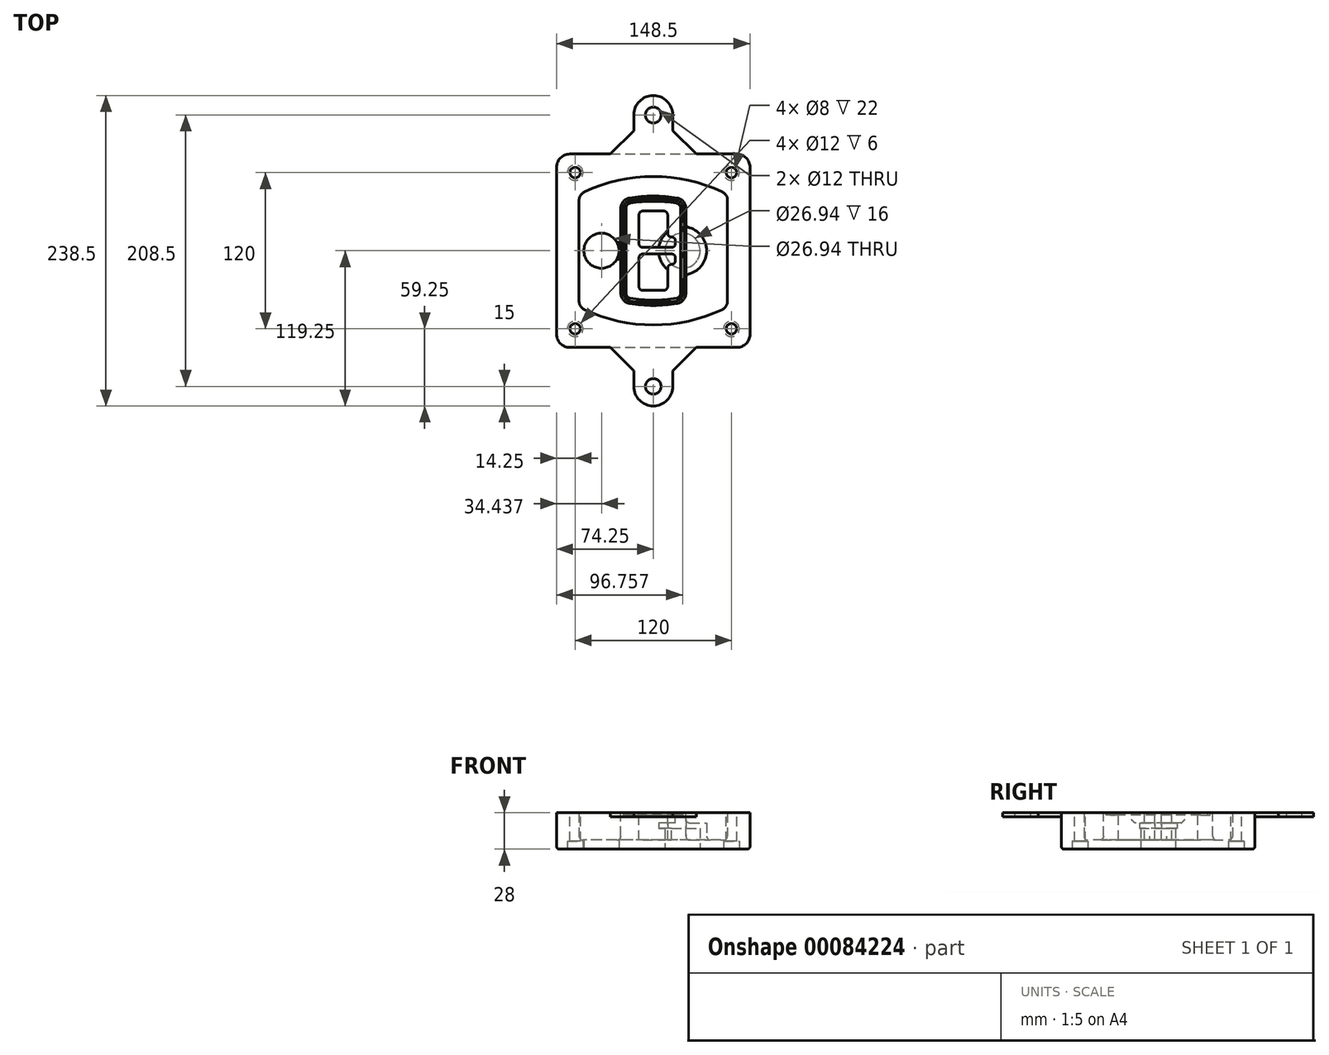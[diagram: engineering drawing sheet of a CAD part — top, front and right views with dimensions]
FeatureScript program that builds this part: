
annotation { "Feature Type Name" : "Feature", "Feature Type Description" : "" }
export const myFeature = defineFeature(function(context is Context, id is Id, definition is map)
    precondition{}
    {
        {
            var Q0;
            Q0=qCreatedBy(makeId("Top.planeOp"),FACE);
            var sketch = newSketch(context, id + "F0", { "sketchPlane" : qUnion([Q0])});
            skPoint(sketch, "E0.rect.middle", {"position": v(0, 0) * mm});
            skLineSegment(sketch, "E1.bottom", {"start": v(-64.25, -74.25) * mm, "end": v(64.25, -74.25) * mm});
            skLineSegment(sketch, "E1.top", {"start": v(-64.25, 74.25) * mm, "end": v(64.25, 74.25) * mm});
            skLineSegment(sketch, "E1.left", {"start": v(-74.25, -64.25) * mm, "end": v(-74.25, 64.25) * mm});
            skLineSegment(sketch, "E1.right", {"start": v(74.25, -64.25) * mm, "end": v(74.25, 64.25) * mm});
            skLineSegment(sketch, "E2", {"start": v(-74.25, 74.25) * mm, "end": v(74.25, -74.25) * mm, "construction": true});
            skLineSegment(sketch, "E3", {"start": v(74.25, 74.25) * mm, "end": v(-74.25, -74.25) * mm, "construction": true});
            skCircle(sketch, "E4", {"center": v(-60, 60) * mm, "radius": 4 * mm});
            skCircle(sketch, "E5", {"center": v(60, 60) * mm, "radius": 4 * mm});
            skCircle(sketch, "E6", {"center": v(60, -60) * mm, "radius": 4 * mm});
            skCircle(sketch, "E7", {"center": v(-60, -60) * mm, "radius": 4 * mm});
            skLineSegment(sketch, "E8", {"start": v(-60, 60) * mm, "end": v(60, 60) * mm, "construction": true});
            skLineSegment(sketch, "E9", {"start": v(60, 60) * mm, "end": v(60, -60) * mm, "construction": true});
            skLineSegment(sketch, "E10", {"start": v(60, -60) * mm, "end": v(-60, -60) * mm, "construction": true});
            skLineSegment(sketch, "E11", {"start": v(-60, -60) * mm, "end": v(-60, 60) * mm, "construction": true});
            skLineSegment(sketch, "E12", {"start": v(-60, 38.83) * mm, "end": v(-60, -38.83) * mm});
            skLineSegment(sketch, "E13", {"start": v(60, 38.83) * mm, "end": v(60, -38.83) * mm});
            skArc(sketch, "E14", {"start": v(54.26, 47.88) * mm, "mid": v(0, 60) * mm, "end": v(-54.26, 47.88) * mm});
            skArc(sketch, "E15", {"start": v(-54.26, -47.88) * mm, "mid": v(0, -60) * mm, "end": v(54.26, -47.88) * mm});
            skLineSegment(sketch, "E16", {"start": v(-60, 0) * mm, "end": v(60, 0) * mm, "construction": true});
            skPoint(sketch, "E17.visualSharp", {"position": v(-60, -45) * mm});
            skArc(sketch, "E17.filletArc", {"start": v(-60, -38.83) * mm, "mid": v(-58.44, -44.2) * mm, "end": v(-54.26, -47.88) * mm});
            skPoint(sketch, "E18.visualSharp", {"position": v(-60, 45) * mm});
            skArc(sketch, "E18.filletArc", {"start": v(-54.26, 47.88) * mm, "mid": v(-58.44, 44.2) * mm, "end": v(-60, 38.83) * mm});
            skPoint(sketch, "E19.visualSharp", {"position": v(60, 45) * mm});
            skArc(sketch, "E19.filletArc", {"start": v(60, 38.83) * mm, "mid": v(58.44, 44.2) * mm, "end": v(54.26, 47.88) * mm});
            skPoint(sketch, "E20.visualSharp", {"position": v(60, -45) * mm});
            skArc(sketch, "E20.filletArc", {"start": v(54.26, -47.88) * mm, "mid": v(58.44, -44.2) * mm, "end": v(60, -38.83) * mm});
            skPoint(sketch, "E21.visualSharp", {"position": v(-74.25, 74.25) * mm});
            skArc(sketch, "E21.filletArc", {"start": v(-64.25, 74.25) * mm, "mid": v(-71.32, 71.32) * mm, "end": v(-74.25, 64.25) * mm});
            skPoint(sketch, "E22.visualSharp", {"position": v(74.25, 74.25) * mm});
            skArc(sketch, "E22.filletArc", {"start": v(74.25, 64.25) * mm, "mid": v(71.32, 71.32) * mm, "end": v(64.25, 74.25) * mm});
            skPoint(sketch, "E23.visualSharp", {"position": v(74.25, -74.25) * mm});
            skArc(sketch, "E23.filletArc", {"start": v(64.25, -74.25) * mm, "mid": v(71.32, -71.32) * mm, "end": v(74.25, -64.25) * mm});
            skPoint(sketch, "E24.visualSharp", {"position": v(-74.25, -74.25) * mm});
            skArc(sketch, "E24.filletArc", {"start": v(-74.25, -64.25) * mm, "mid": v(-71.32, -71.32) * mm, "end": v(-64.25, -74.25) * mm});
            skArc(sketch, "E25.0", {"start": v(57, 38.83) * mm, "mid": v(55.9, 42.58) * mm, "end": v(52.98, 45.17) * mm});
            skLineSegment(sketch, "E25.1", {"start": v(57, 38.83) * mm, "end": v(57, -38.83) * mm});
            skArc(sketch, "E25.2", {"start": v(52.98, -45.17) * mm, "mid": v(55.9, -42.58) * mm, "end": v(57, -38.83) * mm});
            skArc(sketch, "E25.3", {"start": v(-52.98, -45.17) * mm, "mid": v(0, -57) * mm, "end": v(52.98, -45.17) * mm});
            skArc(sketch, "E25.4", {"start": v(-57, -38.83) * mm, "mid": v(-55.9, -42.58) * mm, "end": v(-52.98, -45.17) * mm});
            skArc(sketch, "E25.5", {"start": v(52.98, 45.17) * mm, "mid": v(0, 57) * mm, "end": v(-52.98, 45.17) * mm});
            skLineSegment(sketch, "E25.6", {"start": v(-57, 38.83) * mm, "end": v(-57, -38.83) * mm});
            skArc(sketch, "E25.7", {"start": v(-52.98, 45.17) * mm, "mid": v(-55.9, 42.58) * mm, "end": v(-57, 38.83) * mm});
            skArc(sketch, "E26.0", {"start": v(-55.96, 51.5) * mm, "mid": v(-61.82, 46.33) * mm, "end": v(-64, 38.83) * mm});
            skArc(sketch, "E26.1", {"start": v(55.96, 51.5) * mm, "mid": v(0, 64) * mm, "end": v(-55.96, 51.5) * mm});
            skArc(sketch, "E26.2", {"start": v(64, 38.83) * mm, "mid": v(61.82, 46.33) * mm, "end": v(55.96, 51.5) * mm});
            skLineSegment(sketch, "E26.3", {"start": v(64, 38.83) * mm, "end": v(64, -38.83) * mm});
            skArc(sketch, "E26.4", {"start": v(55.96, -51.5) * mm, "mid": v(61.82, -46.33) * mm, "end": v(64, -38.83) * mm});
            skLineSegment(sketch, "E26.5", {"start": v(-64, 38.83) * mm, "end": v(-64, -38.83) * mm});
            skArc(sketch, "E26.6", {"start": v(-55.96, -51.5) * mm, "mid": v(0, -64) * mm, "end": v(55.96, -51.5) * mm});
            skArc(sketch, "E26.7", {"start": v(-64, -38.83) * mm, "mid": v(-61.82, -46.33) * mm, "end": v(-55.96, -51.5) * mm});
            skSolve(sketch);
        }
        {
            var Q0;
            Q0=makeQuery(id+"F0.imprint","IMPRINT",FACE,{"disambiguationData":[TD([[makeQuery(id+"F0.imprint","IMPRINT",EDGE,{"derivedFrom":sQuery(id+"F0.wireOp",EDGE,"E1.bottom")}),1.0]])]});
            var Q1;
            Q1=makeQuery(id+"F0.imprint","IMPRINT",FACE,{"disambiguationData":[TD([[makeQuery(id+"F0.imprint","IMPRINT",EDGE,{"derivedFrom":sQuery(id+"F0.wireOp",EDGE,"E12")}),1.0]])]});
            var Q2;
            Q2=makeQuery(id+"F0.imprint","IMPRINT",FACE,{"disambiguationData":[TD([[makeQuery(id+"F0.imprint","IMPRINT",EDGE,{"derivedFrom":sQuery(id+"F0.wireOp",EDGE,"E25.0")}),1.0]])]});
            var Q3;
            Q3=makeQuery(id+"F0.imprint","IMPRINT",FACE,{"disambiguationData":[TD([[makeQuery(id+"F0.imprint","IMPRINT",EDGE,{"derivedFrom":sQuery(id+"F0.wireOp",EDGE,"E12")}),-1.0]])]});
            extrude(context, id + "F1", {"entities" : qUnion([Q0, Q1, Q2, Q3]), "oppositeDirection" : true, "depth" : 25 * mm});
        }
        {
            var Q0;
            Q0=makeQuery(id+"F0.imprint","IMPRINT",FACE,{"disambiguationData":[TD([[makeQuery(id+"F0.imprint","IMPRINT",EDGE,{"derivedFrom":sQuery(id+"F0.wireOp",EDGE,"E12")}),1.0]])]});
            extrude(context, id + "F2", {"entities" : qUnion([Q0]), "operationType" : NewBodyOperationType.ADD, "depth" : 3 * mm});
        }
        {
            var Q0;
            Q0=makeQuery(id+"F0.imprint","IMPRINT",FACE,{"disambiguationData":[TD([[makeQuery(id+"F0.imprint","IMPRINT",EDGE,{"derivedFrom":sQuery(id+"F0.wireOp",EDGE,"E25.0")}),1.0]])]});
            extrude(context, id + "F3", {"entities" : qUnion([Q0]), "operationType" : NewBodyOperationType.REMOVE, "oppositeDirection" : true, "depth" : 18 * mm});
        }
        {
            var Q0;
            Q0=makeQuery(id+"F2.opExtrude","CAP_FACE",FACE,{"disambiguationData":[OSD([sQuery(id+"F0.wireOp",EDGE,"E12"),sQuery(id+"F0.wireOp",EDGE,"E13"),sQuery(id+"F0.wireOp",EDGE,"E14"),sQuery(id+"F0.wireOp",EDGE,"E15"),sQuery(id+"F0.wireOp",EDGE,"E17.filletArc"),sQuery(id+"F0.wireOp",EDGE,"E18.filletArc"),sQuery(id+"F0.wireOp",EDGE,"E19.filletArc"),sQuery(id+"F0.wireOp",EDGE,"E20.filletArc"),sQuery(id+"F0.wireOp",EDGE,"E25.0"),sQuery(id+"F0.wireOp",EDGE,"E25.1"),sQuery(id+"F0.wireOp",EDGE,"E25.2"),sQuery(id+"F0.wireOp",EDGE,"E25.3"),sQuery(id+"F0.wireOp",EDGE,"E25.4"),sQuery(id+"F0.wireOp",EDGE,"E25.5"),sQuery(id+"F0.wireOp",EDGE,"E25.6"),sQuery(id+"F0.wireOp",EDGE,"E25.7")])],"isStart":false});
            var sketch = newSketch(context, id + "F4", { "sketchPlane" : qUnion([Q0])});
            skArc(sketch, "E27.0", {"start": v(-18.34, -40.45) * mm, "mid": v(0, -42) * mm, "end": v(18.34, -40.45) * mm});
            skArc(sketch, "E28.0", {"start": v(18.34, 40.45) * mm, "mid": v(0, 42) * mm, "end": v(-18.34, 40.45) * mm});
            skLineSegment(sketch, "E29", {"start": v(-25, 32.57) * mm, "end": v(-25, -32.57) * mm});
            skLineSegment(sketch, "E30", {"start": v(25, 32.57) * mm, "end": v(25, -32.57) * mm});
            skLineSegment(sketch, "E31", {"start": v(-25, 39.1) * mm, "end": v(25, 39.1) * mm, "construction": true});
            skLineSegment(sketch, "E32", {"start": v(-25, -39.1) * mm, "end": v(25, -39.1) * mm, "construction": true});
            skPoint(sketch, "E33.visualSharp", {"position": v(-25, 39.1) * mm});
            skArc(sketch, "E33.filletArc", {"start": v(-18.34, 40.45) * mm, "mid": v(-23.11, 37.73) * mm, "end": v(-25, 32.57) * mm});
            skPoint(sketch, "E34.visualSharp", {"position": v(25, 39.1) * mm});
            skArc(sketch, "E34.filletArc", {"start": v(25, 32.57) * mm, "mid": v(23.11, 37.73) * mm, "end": v(18.34, 40.45) * mm});
            skPoint(sketch, "E35.visualSharp", {"position": v(25, -39.1) * mm});
            skArc(sketch, "E35.filletArc", {"start": v(18.34, -40.45) * mm, "mid": v(23.11, -37.73) * mm, "end": v(25, -32.57) * mm});
            skPoint(sketch, "E36.visualSharp", {"position": v(-25, -39.1) * mm});
            skArc(sketch, "E36.filletArc", {"start": v(-25, -32.57) * mm, "mid": v(-23.11, -37.73) * mm, "end": v(-18.34, -40.45) * mm});
            skArc(sketch, "E37.0", {"start": v(52.98, 45.17) * mm, "mid": v(0, 57) * mm, "end": v(-52.98, 45.17) * mm});
            skArc(sketch, "E37.1", {"start": v(-52.98, 45.17) * mm, "mid": v(-55.9, 42.58) * mm, "end": v(-57, 38.83) * mm});
            skLineSegment(sketch, "E37.2", {"start": v(-57, 38.83) * mm, "end": v(-57, -38.83) * mm});
            skArc(sketch, "E37.3", {"start": v(-57, -38.83) * mm, "mid": v(-55.9, -42.58) * mm, "end": v(-52.98, -45.17) * mm});
            skArc(sketch, "E37.4", {"start": v(-52.98, -45.17) * mm, "mid": v(0, -57) * mm, "end": v(52.98, -45.17) * mm});
            skArc(sketch, "E37.5", {"start": v(52.98, -45.17) * mm, "mid": v(55.9, -42.58) * mm, "end": v(57, -38.83) * mm});
            skLineSegment(sketch, "E37.6", {"start": v(57, 38.83) * mm, "end": v(57, -38.83) * mm});
            skArc(sketch, "E37.7", {"start": v(57, 38.83) * mm, "mid": v(55.9, 42.58) * mm, "end": v(52.98, 45.17) * mm});
            skLineSegment(sketch, "E38.0", {"start": v(23, 32.57) * mm, "end": v(23, -32.57) * mm});
            skArc(sketch, "E38.1", {"start": v(18, -38.48) * mm, "mid": v(21.58, -36.44) * mm, "end": v(23, -32.57) * mm});
            skArc(sketch, "E38.2", {"start": v(-18, -38.48) * mm, "mid": v(0, -40) * mm, "end": v(18, -38.48) * mm});
            skArc(sketch, "E38.3", {"start": v(-23, -32.57) * mm, "mid": v(-21.58, -36.44) * mm, "end": v(-18, -38.48) * mm});
            skLineSegment(sketch, "E38.4", {"start": v(-23, 32.57) * mm, "end": v(-23, -32.57) * mm});
            skArc(sketch, "E38.5", {"start": v(23, 32.57) * mm, "mid": v(21.58, 36.44) * mm, "end": v(18, 38.48) * mm});
            skArc(sketch, "E38.6", {"start": v(-18, 38.48) * mm, "mid": v(-21.58, 36.44) * mm, "end": v(-23, 32.57) * mm});
            skArc(sketch, "E38.7", {"start": v(18, 38.48) * mm, "mid": v(0, 40) * mm, "end": v(-18, 38.48) * mm});
            skArc(sketch, "E39.0", {"start": v(21, 32.57) * mm, "mid": v(20.06, 35.15) * mm, "end": v(17.67, 36.5) * mm});
            skLineSegment(sketch, "E39.1", {"start": v(21, 32.57) * mm, "end": v(21, -32.57) * mm});
            skArc(sketch, "E39.2", {"start": v(17.67, -36.5) * mm, "mid": v(20.06, -35.15) * mm, "end": v(21, -32.57) * mm});
            skArc(sketch, "E39.3", {"start": v(-17.67, -36.5) * mm, "mid": v(0, -38) * mm, "end": v(17.67, -36.5) * mm});
            skArc(sketch, "E39.4", {"start": v(-21, -32.57) * mm, "mid": v(-20.06, -35.15) * mm, "end": v(-17.67, -36.5) * mm});
            skArc(sketch, "E39.5", {"start": v(17.67, 36.5) * mm, "mid": v(0, 38) * mm, "end": v(-17.67, 36.5) * mm});
            skLineSegment(sketch, "E39.6", {"start": v(-21, 32.57) * mm, "end": v(-21, -32.57) * mm});
            skArc(sketch, "E39.7", {"start": v(-17.67, 36.5) * mm, "mid": v(-20.06, 35.15) * mm, "end": v(-21, 32.57) * mm});
            skLineSegment(sketch, "E40", {"start": v(-25, 0) * mm, "end": v(25, 0) * mm, "construction": true});
            skLineSegment(sketch, "E41", {"start": v(-11, 5.5) * mm, "end": v(-11, 27.5) * mm});
            skLineSegment(sketch, "E42", {"start": v(-8, 30.5) * mm, "end": v(8, 30.5) * mm});
            skLineSegment(sketch, "E43", {"start": v(11, 27.5) * mm, "end": v(11, 13.5) * mm});
            skLineSegment(sketch, "E44", {"start": v(14, 10.5) * mm, "end": v(14, 10.5) * mm});
            skLineSegment(sketch, "E45", {"start": v(17, 7.5) * mm, "end": v(17, 5.5) * mm});
            skLineSegment(sketch, "E46", {"start": v(14, 2.5) * mm, "end": v(-8, 2.5) * mm});
            skPoint(sketch, "E47.visualSharp", {"position": v(-11, 30.5) * mm});
            skArc(sketch, "E47.filletArc", {"start": v(-8, 30.5) * mm, "mid": v(-10.12, 29.62) * mm, "end": v(-11, 27.5) * mm});
            skPoint(sketch, "E48.visualSharp", {"position": v(11, 30.5) * mm});
            skArc(sketch, "E48.filletArc", {"start": v(11, 27.5) * mm, "mid": v(10.12, 29.62) * mm, "end": v(8, 30.5) * mm});
            skPoint(sketch, "E49.visualSharp", {"position": v(11, 10.5) * mm});
            skArc(sketch, "E49.filletArc", {"start": v(11, 13.5) * mm, "mid": v(11.88, 11.38) * mm, "end": v(14, 10.5) * mm});
            skPoint(sketch, "E50.visualSharp", {"position": v(17, 10.5) * mm});
            skArc(sketch, "E50.filletArc", {"start": v(17, 7.5) * mm, "mid": v(16.12, 9.62) * mm, "end": v(14, 10.5) * mm});
            skPoint(sketch, "E51.visualSharp", {"position": v(17, 2.5) * mm});
            skArc(sketch, "E51.filletArc", {"start": v(14, 2.5) * mm, "mid": v(16.12, 3.38) * mm, "end": v(17, 5.5) * mm});
            skPoint(sketch, "E52.visualSharp", {"position": v(-11, 2.5) * mm});
            skArc(sketch, "E52.filletArc", {"start": v(-11, 5.5) * mm, "mid": v(-10.12, 3.38) * mm, "end": v(-8, 2.5) * mm});
            skLineSegment(sketch, "E53.0.MirrorCS", {"start": v(14, -2.5) * mm, "end": v(-8, -2.5) * mm});
            skArc(sketch, "E54.0.MirrorCS", {"start": v(-11, -5.5) * mm, "mid": v(-10.12, -3.38) * mm, "end": v(-8, -2.5) * mm});
            skLineSegment(sketch, "E55.0.MirrorCS", {"start": v(-11, -5.5) * mm, "end": v(-11, -27.5) * mm});
            skArc(sketch, "E56.0.MirrorCS", {"start": v(-8, -30.5) * mm, "mid": v(-10.12, -29.62) * mm, "end": v(-11, -27.5) * mm});
            skLineSegment(sketch, "E57.0.MirrorCS", {"start": v(-8, -30.5) * mm, "end": v(8, -30.5) * mm});
            skArc(sketch, "E58.0.MirrorCS", {"start": v(11, -27.5) * mm, "mid": v(10.12, -29.62) * mm, "end": v(8, -30.5) * mm});
            skLineSegment(sketch, "E59.0.MirrorCS", {"start": v(11, -27.5) * mm, "end": v(11, -13.5) * mm});
            skArc(sketch, "E60.0.MirrorCS", {"start": v(11, -13.5) * mm, "mid": v(11.88, -11.38) * mm, "end": v(14, -10.5) * mm});
            skArc(sketch, "E61.0.MirrorCS", {"start": v(17, -7.5) * mm, "mid": v(16.12, -9.62) * mm, "end": v(14, -10.5) * mm});
            skLineSegment(sketch, "E62.0.MirrorCS", {"start": v(17, -7.5) * mm, "end": v(17, -5.5) * mm});
            skArc(sketch, "E63.0.MirrorCS", {"start": v(14, -2.5) * mm, "mid": v(16.12, -3.38) * mm, "end": v(17, -5.5) * mm});
            skSolve(sketch);
        }
        {
            var Q0;
            Q0=makeQuery(id+"F4.imprint","IMPRINT",FACE,{"disambiguationData":[TD([[makeQuery(id+"F4.imprint","IMPRINT",EDGE,{"derivedFrom":sQuery(id+"F4.wireOp",EDGE,"E27.0")}),1.0]])]});
            var Q1;
            Q1=makeQuery(id+"F4.imprint","IMPRINT",FACE,{"disambiguationData":[TD([[makeQuery(id+"F4.imprint","IMPRINT",EDGE,{"derivedFrom":sQuery(id+"F4.wireOp",EDGE,"E38.0")}),-1.0]])]});
            var Q2;
            Q2=makeQuery(id+"F4.imprint","IMPRINT",FACE,{"disambiguationData":[TD([[makeQuery(id+"F4.imprint","IMPRINT",EDGE,{"derivedFrom":sQuery(id+"F4.wireOp",EDGE,"E39.0")}),1.0]])]});
            extrude(context, id + "F5", {"entities" : qUnion([Q0, Q1, Q2]), "operationType" : NewBodyOperationType.ADD, "endBound" : BoundingType.UP_TO_NEXT, "oppositeDirection" : true, "depth" : 25 * mm});
        }
        {
            var Q0;
            Q0=makeQuery(id+"F4.imprint","IMPRINT",FACE,{"disambiguationData":[TD([[makeQuery(id+"F4.imprint","IMPRINT",EDGE,{"derivedFrom":sQuery(id+"F4.wireOp",EDGE,"E38.0")}),-1.0]])]});
            extrude(context, id + "F6", {"entities" : qUnion([Q0]), "operationType" : NewBodyOperationType.REMOVE, "oppositeDirection" : true, "depth" : 2 * mm});
        }
        {
            var Q0;
            Q0=makeQuery(id+"F1.opExtrude","CAP_FACE",FACE,{"disambiguationData":[OSD([sQuery(id+"F0.wireOp",EDGE,"E1.bottom"),sQuery(id+"F0.wireOp",EDGE,"E1.top"),sQuery(id+"F0.wireOp",EDGE,"E1.left"),sQuery(id+"F0.wireOp",EDGE,"E1.right"),sQuery(id+"F0.wireOp",EDGE,"E4"),sQuery(id+"F0.wireOp",EDGE,"E5"),sQuery(id+"F0.wireOp",EDGE,"E6"),sQuery(id+"F0.wireOp",EDGE,"E7"),sQuery(id+"F0.wireOp",EDGE,"E21.filletArc"),sQuery(id+"F0.wireOp",EDGE,"E22.filletArc"),sQuery(id+"F0.wireOp",EDGE,"E23.filletArc"),sQuery(id+"F0.wireOp",EDGE,"E24.filletArc")])],"isStart":false});
            var sketch = newSketch(context, id + "F7", { "sketchPlane" : qUnion([Q0])});
            skCircle(sketch, "E64", {"center": v(22.5, 0) * mm, "radius": 13.47 * mm});
            skCircle(sketch, "E65", {"center": v(-39.81, 0) * mm, "radius": 13.47 * mm});
            skLineSegment(sketch, "E66", {"start": v(74.25, 0) * mm, "end": v(-74.25, 0) * mm});
            skCircle(sketch, "E67", {"center": v(22.5, 0) * mm, "radius": 18.47 * mm});
            skCircle(sketch, "E68", {"center": v(60, -60) * mm, "radius": 6 * mm});
            skCircle(sketch, "E69", {"center": v(-60, -60) * mm, "radius": 6 * mm});
            skCircle(sketch, "E70", {"center": v(-60, 60) * mm, "radius": 6 * mm});
            skCircle(sketch, "E71", {"center": v(60, 60) * mm, "radius": 6 * mm});
            skSolve(sketch);
        }
        {
            var Q0;
            {var subQ1=sQuery(id+"F7.wireOp",EDGE,"E66");var subQ4=sQuery(id+"F7.wireOp",EDGE,"E64");var subQ6=makeQuery(id+"F7.imprint","INTERSECT",VERTEX,{"disambiguationData":[OD(0.0)],"derivedFrom":[subQ4,subQ1]});Q0=makeQuery(id+"F7.imprint","IMPRINT",FACE,{"disambiguationData":[TD([[makeQuery(id+"F7.imprint","IMPRINT",EDGE,{"disambiguationData":[TD([[subQ6,-1.0]])],"derivedFrom":subQ4}),-1.0]])]});}
            var Q1;
            {var subQ0=sQuery(id+"F7.wireOp",EDGE,"E66");var subQ1=sQuery(id+"F7.wireOp",EDGE,"E64");var subQ3=makeQuery(id+"F7.imprint","INTERSECT",VERTEX,{"disambiguationData":[OD(0.0)],"derivedFrom":[subQ1,subQ0]});Q1=makeQuery(id+"F7.imprint","IMPRINT",FACE,{"disambiguationData":[TD([[makeQuery(id+"F7.imprint","IMPRINT",EDGE,{"disambiguationData":[TD([[subQ3,-1.0]])],"derivedFrom":subQ1}),1.0]])]});}
            var Q2;
            {var subQ0=sQuery(id+"F7.wireOp",EDGE,"E66");var subQ1=sQuery(id+"F7.wireOp",EDGE,"E64");var subQ3=makeQuery(id+"F7.imprint","INTERSECT",VERTEX,{"disambiguationData":[OD(0.0)],"derivedFrom":[subQ1,subQ0]});Q2=makeQuery(id+"F7.imprint","IMPRINT",FACE,{"disambiguationData":[TD([[makeQuery(id+"F7.imprint","IMPRINT",EDGE,{"disambiguationData":[TD([[subQ3,1.0]])],"derivedFrom":subQ1}),1.0]])]});}
            var Q3;
            {var subQ1=sQuery(id+"F7.wireOp",EDGE,"E66");var subQ4=sQuery(id+"F7.wireOp",EDGE,"E64");var subQ6=makeQuery(id+"F7.imprint","INTERSECT",VERTEX,{"disambiguationData":[OD(0.0)],"derivedFrom":[subQ4,subQ1]});Q3=makeQuery(id+"F7.imprint","IMPRINT",FACE,{"disambiguationData":[TD([[makeQuery(id+"F7.imprint","IMPRINT",EDGE,{"disambiguationData":[TD([[subQ6,1.0]])],"derivedFrom":subQ4}),-1.0]])]});}
            extrude(context, id + "F8", {"entities" : qUnion([Q0, Q1, Q2, Q3]), "operationType" : NewBodyOperationType.ADD, "oppositeDirection" : true, "depth" : 20 * mm});
        }
        {
            var Q0;
            {var subQ0=sQuery(id+"F7.wireOp",EDGE,"E66");var subQ1=sQuery(id+"F7.wireOp",EDGE,"E64");var subQ3=makeQuery(id+"F7.imprint","INTERSECT",VERTEX,{"disambiguationData":[OD(0.0)],"derivedFrom":[subQ1,subQ0]});Q0=makeQuery(id+"F7.imprint","IMPRINT",FACE,{"disambiguationData":[TD([[makeQuery(id+"F7.imprint","IMPRINT",EDGE,{"disambiguationData":[TD([[subQ3,-1.0]])],"derivedFrom":subQ1}),1.0]])]});}
            var Q1;
            {var subQ0=sQuery(id+"F7.wireOp",EDGE,"E66");var subQ1=sQuery(id+"F7.wireOp",EDGE,"E64");var subQ3=makeQuery(id+"F7.imprint","INTERSECT",VERTEX,{"disambiguationData":[OD(0.0)],"derivedFrom":[subQ1,subQ0]});Q1=makeQuery(id+"F7.imprint","IMPRINT",FACE,{"disambiguationData":[TD([[makeQuery(id+"F7.imprint","IMPRINT",EDGE,{"disambiguationData":[TD([[subQ3,1.0]])],"derivedFrom":subQ1}),1.0]])]});}
            extrude(context, id + "F9", {"entities" : qUnion([Q0, Q1]), "operationType" : NewBodyOperationType.REMOVE, "oppositeDirection" : true, "depth" : 16 * mm});
        }
        {
            var Q0;
            {var subQ0=sQuery(id+"F7.wireOp",EDGE,"E66");var subQ1=sQuery(id+"F7.wireOp",EDGE,"E65");var subQ3=makeQuery(id+"F7.imprint","INTERSECT",VERTEX,{"disambiguationData":[OD(0.0)],"derivedFrom":[subQ1,subQ0]});Q0=makeQuery(id+"F7.imprint","IMPRINT",FACE,{"disambiguationData":[TD([[makeQuery(id+"F7.imprint","IMPRINT",EDGE,{"disambiguationData":[TD([[subQ3,-1.0]])],"derivedFrom":subQ1}),1.0]])]});}
            var Q1;
            {var subQ0=sQuery(id+"F7.wireOp",EDGE,"E66");var subQ1=sQuery(id+"F7.wireOp",EDGE,"E65");var subQ3=makeQuery(id+"F7.imprint","INTERSECT",VERTEX,{"disambiguationData":[OD(0.0)],"derivedFrom":[subQ1,subQ0]});Q1=makeQuery(id+"F7.imprint","IMPRINT",FACE,{"disambiguationData":[TD([[makeQuery(id+"F7.imprint","IMPRINT",EDGE,{"disambiguationData":[TD([[subQ3,1.0]])],"derivedFrom":subQ1}),1.0]])]});}
            extrude(context, id + "F10", {"entities" : qUnion([Q0, Q1]), "operationType" : NewBodyOperationType.REMOVE, "oppositeDirection" : true, "depth" : 25 * mm});
        }
        {
            var Q0;
            Q0=makeQuery(id+"F7.imprint","IMPRINT",FACE,{"disambiguationData":[TD([[makeQuery(id+"F7.imprint","IMPRINT",EDGE,{"derivedFrom":sQuery(id+"F7.wireOp",EDGE,"E68")}),1.0]])]});
            var Q1;
            Q1=makeQuery(id+"F7.imprint","IMPRINT",FACE,{"disambiguationData":[TD([[makeQuery(id+"F7.imprint","IMPRINT",EDGE,{"derivedFrom":makeQuery(id+"F1.opExtrude","CAP_EDGE",EDGE,{"disambiguationData":[OSD([sQuery(id+"F0.wireOp",EDGE,"E5")])],"isStart":false})}),-1.0]])]});
            var Q2;
            Q2=makeQuery(id+"F7.imprint","IMPRINT",FACE,{"disambiguationData":[TD([[makeQuery(id+"F7.imprint","IMPRINT",EDGE,{"derivedFrom":sQuery(id+"F7.wireOp",EDGE,"E69")}),1.0]])]});
            var Q3;
            Q3=makeQuery(id+"F7.imprint","IMPRINT",FACE,{"disambiguationData":[TD([[makeQuery(id+"F7.imprint","IMPRINT",EDGE,{"derivedFrom":makeQuery(id+"F1.opExtrude","CAP_EDGE",EDGE,{"disambiguationData":[OSD([sQuery(id+"F0.wireOp",EDGE,"E4")])],"isStart":false})}),-1.0]])]});
            var Q4;
            Q4=makeQuery(id+"F7.imprint","IMPRINT",FACE,{"disambiguationData":[TD([[makeQuery(id+"F7.imprint","IMPRINT",EDGE,{"derivedFrom":sQuery(id+"F7.wireOp",EDGE,"E70")}),1.0]])]});
            var Q5;
            Q5=makeQuery(id+"F7.imprint","IMPRINT",FACE,{"disambiguationData":[TD([[makeQuery(id+"F7.imprint","IMPRINT",EDGE,{"derivedFrom":makeQuery(id+"F1.opExtrude","CAP_EDGE",EDGE,{"disambiguationData":[OSD([sQuery(id+"F0.wireOp",EDGE,"E7")])],"isStart":false})}),-1.0]])]});
            var Q6;
            Q6=makeQuery(id+"F7.imprint","IMPRINT",FACE,{"disambiguationData":[TD([[makeQuery(id+"F7.imprint","IMPRINT",EDGE,{"derivedFrom":sQuery(id+"F7.wireOp",EDGE,"E71")}),1.0]])]});
            var Q7;
            Q7=makeQuery(id+"F7.imprint","IMPRINT",FACE,{"disambiguationData":[TD([[makeQuery(id+"F7.imprint","IMPRINT",EDGE,{"derivedFrom":makeQuery(id+"F1.opExtrude","CAP_EDGE",EDGE,{"disambiguationData":[OSD([sQuery(id+"F0.wireOp",EDGE,"E6")])],"isStart":false})}),-1.0]])]});
            extrude(context, id + "F11", {"entities" : qUnion([Q0, Q1, Q2, Q3, Q4, Q5, Q6, Q7]), "operationType" : NewBodyOperationType.REMOVE, "oppositeDirection" : true, "depth" : 6 * mm});
        }
        {
            var Q0;
            Q0=makeQuery(id+"F9.boolean.opBoolean","COPY",FACE,{"derivedFrom":makeQuery(id+"F9.opExtrude","CAP_FACE",FACE,{"disambiguationData":[OSD([sQuery(id+"F7.wireOp",EDGE,"E64")])],"isStart":false})});
            var sketch = newSketch(context, id + "F12", { "sketchPlane" : qUnion([Q0])});
            skArc(sketch, "E72.0", {"start": v(11, 14.45) * mm, "mid": v(6.45, 9.13) * mm, "end": v(4.2, 2.5) * mm});
            skArc(sketch, "E72.1", {"start": v(4.2, -2.5) * mm, "mid": v(6.45, -9.13) * mm, "end": v(11, -14.45) * mm});
            skLineSegment(sketch, "E73", {"start": v(4.2, -2.5) * mm, "end": v(14, -2.5) * mm});
            skLineSegment(sketch, "E74.0", {"start": v(14, 2.5) * mm, "end": v(4.2, 2.5) * mm});
            skArc(sketch, "E74.1", {"start": v(14, 2.5) * mm, "mid": v(16.12, 3.38) * mm, "end": v(17, 5.5) * mm});
            skLineSegment(sketch, "E74.2", {"start": v(17, 7.5) * mm, "end": v(17, 5.5) * mm});
            skArc(sketch, "E74.3", {"start": v(17, 7.5) * mm, "mid": v(16.12, 9.62) * mm, "end": v(14, 10.5) * mm});
            skArc(sketch, "E74.4", {"start": v(11, 13.5) * mm, "mid": v(11.88, 11.38) * mm, "end": v(14, 10.5) * mm});
            skLineSegment(sketch, "E74.5", {"start": v(11, 14.45) * mm, "end": v(11, 13.5) * mm});
            skLineSegment(sketch, "E74.7", {"start": v(14, -2.5) * mm, "end": v(4.2, -2.5) * mm});
            skArc(sketch, "E74.8", {"start": v(14, -2.5) * mm, "mid": v(16.12, -3.38) * mm, "end": v(17, -5.5) * mm});
            skLineSegment(sketch, "E74.9", {"start": v(17, -7.5) * mm, "end": v(17, -5.5) * mm});
            skArc(sketch, "E74.10", {"start": v(17, -7.5) * mm, "mid": v(16.12, -9.62) * mm, "end": v(14, -10.5) * mm});
            skArc(sketch, "E74.11", {"start": v(11, -13.5) * mm, "mid": v(11.88, -11.38) * mm, "end": v(14, -10.5) * mm});
            skLineSegment(sketch, "E74.12", {"start": v(11, -14.45) * mm, "end": v(11, -13.5) * mm});
            skPoint(sketch, "E75.orphan", {"position": v(11, -27.5) * mm});
            skPoint(sketch, "E76.orphan", {"position": v(-8, -2.5) * mm});
            skPoint(sketch, "E77.orphan", {"position": v(-8, 2.5) * mm});
            skPoint(sketch, "E78.orphan", {"position": v(11, 27.5) * mm});
            skSolve(sketch);
        }
        {
            var Q0;
            {var subQ7=sQuery(id+"F12.wireOp",EDGE,"E72.0");var subQ14=sQuery(id+"F12.wireOp",EDGE,"E72.1");var subQ16=sQuery(id+"F12.wireOp",EDGE,"E74.1");var subQ18=sQuery(id+"F12.wireOp",EDGE,"E74.8");Q0=qUnion([makeQuery(id+"F12.imprint","IMPRINT",FACE,{"disambiguationData":[TD([[makeQuery(id+"F12.imprint","IMPRINT",EDGE,{"derivedFrom":subQ7}),1.0]])]}),makeQuery(id+"F12.imprint","IMPRINT",FACE,{"disambiguationData":[TD([[makeQuery(id+"F12.imprint","IMPRINT",EDGE,{"derivedFrom":subQ14}),1.0]])]}),makeQuery(id+"F12.imprint","IMPRINT",FACE,{"disambiguationData":[TD([[makeQuery(id+"F12.imprint","IMPRINT",EDGE,{"derivedFrom":subQ16}),1.0]])]}),makeQuery(id+"F12.imprint","IMPRINT",FACE,{"disambiguationData":[TD([[makeQuery(id+"F12.imprint","IMPRINT",EDGE,{"derivedFrom":subQ18}),-1.0]])]})]);}
            var Q1;
            Q1=makeQuery(id+"F5.boolean.opBoolean","SPLIT",FACE,{"disambiguationData":[TD([makeQuery(id+"F5.opExtrude","SWEPT_FACE",FACE,{"disambiguationData":[OSD([sQuery(id+"F4.wireOp",EDGE,"E41")])]})])],"derivedFrom":makeQuery(id+"F3.boolean.opBoolean","COPY",FACE,{"derivedFrom":makeQuery(id+"F3.opExtrude","CAP_FACE",FACE,{"disambiguationData":[OSD([sQuery(id+"F0.wireOp",EDGE,"E25.0"),sQuery(id+"F0.wireOp",EDGE,"E25.1"),sQuery(id+"F0.wireOp",EDGE,"E25.2"),sQuery(id+"F0.wireOp",EDGE,"E25.3"),sQuery(id+"F0.wireOp",EDGE,"E25.4"),sQuery(id+"F0.wireOp",EDGE,"E25.5"),sQuery(id+"F0.wireOp",EDGE,"E25.6"),sQuery(id+"F0.wireOp",EDGE,"E25.7")])],"isStart":false})})});
            extrude(context, id + "F13", {"entities" : qUnion([Q0]), "operationType" : NewBodyOperationType.REMOVE, "endBound" : BoundingType.UP_TO_SURFACE, "endBoundEntityFace" : qUnion([Q1]), "depth" : 25 * mm});
        }
        {
            var Q0;
            Q0=makeQuery(id+"F3.boolean.opBoolean","COPY",EDGE,{"derivedFrom":makeQuery(id+"F3.opExtrude","CAP_EDGE",EDGE,{"disambiguationData":[OSD([sQuery(id+"F0.wireOp",EDGE,"E25.6")])],"isStart":false})});
            var Q1;
            Q1=makeQuery(id+"F8.boolean.opBoolean","INTERSECT",EDGE,{"derivedFrom":[makeQuery(id+"F5.opExtrude","SWEPT_FACE",FACE,{"disambiguationData":[OSD([sQuery(id+"F4.wireOp",EDGE,"E30")])]}),makeQuery(id+"F8.opExtrude","CAP_FACE",FACE,{"disambiguationData":[OSD([sQuery(id+"F7.wireOp",EDGE,"E67")])],"isStart":false})]});
            var Q2;
            Q2=makeQuery(id+"F8.boolean.opBoolean","INTERSECT",EDGE,{"disambiguationData":[OD(1.0)],"derivedFrom":[makeQuery(id+"F5.opExtrude","SWEPT_FACE",FACE,{"disambiguationData":[OSD([sQuery(id+"F4.wireOp",EDGE,"E30")])]}),makeQuery(id+"F8.opExtrude","SWEPT_FACE",FACE,{"disambiguationData":[OSD([sQuery(id+"F7.wireOp",EDGE,"E67")])]})]});
            var Q3;
            {var subQ0=sQuery(id+"F4.wireOp",EDGE,"E30");Q3=makeQuery(id+"F8.boolean.opBoolean","SPLIT",EDGE,{"disambiguationData":[TD([makeQuery(id+"F5.opExtrude","SWEPT_FACE",FACE,{"disambiguationData":[OSD([sQuery(id+"F4.wireOp",EDGE,"E35.filletArc")])]})])],"derivedFrom":makeQuery(id+"F5.opExtrude","CAP_EDGE",EDGE,{"disambiguationData":[OSD([subQ0])],"isStart":false})});}
            var Q4;
            {var subQ0=sQuery(id+"F0.wireOp",EDGE,"E25.7");var subQ1=sQuery(id+"F0.wireOp",EDGE,"E25.1");var subQ2=sQuery(id+"F0.wireOp",EDGE,"E25.6");var subQ3=sQuery(id+"F0.wireOp",EDGE,"E25.5");var subQ4=sQuery(id+"F0.wireOp",EDGE,"E25.4");var subQ5=sQuery(id+"F0.wireOp",EDGE,"E25.0");var subQ6=sQuery(id+"F0.wireOp",EDGE,"E25.2");var subQ7=sQuery(id+"F0.wireOp",EDGE,"E25.3");Q4=makeQuery(id+"F8.boolean.opBoolean","INTERSECT",EDGE,{"derivedFrom":[makeQuery(id+"F5.boolean.opBoolean","SPLIT",FACE,{"disambiguationData":[TD([makeQuery(id+"F2.opExtrude","SWEPT_FACE",FACE,{"disambiguationData":[OSD([subQ5])]})])],"derivedFrom":makeQuery(id+"F3.boolean.opBoolean","COPY",FACE,{"derivedFrom":makeQuery(id+"F3.opExtrude","CAP_FACE",FACE,{"disambiguationData":[OSD([subQ5,subQ1,subQ6,subQ7,subQ4,subQ3,subQ2,subQ0])],"isStart":false})})}),makeQuery(id+"F8.opExtrude","SWEPT_FACE",FACE,{"disambiguationData":[OSD([sQuery(id+"F7.wireOp",EDGE,"E67")])]})]});}
            var Q5;
            Q5=makeQuery(id+"F8.boolean.opBoolean","INTERSECT",EDGE,{"disambiguationData":[OD(0.0)],"derivedFrom":[makeQuery(id+"F5.opExtrude","SWEPT_FACE",FACE,{"disambiguationData":[OSD([sQuery(id+"F4.wireOp",EDGE,"E30")])]}),makeQuery(id+"F8.opExtrude","SWEPT_FACE",FACE,{"disambiguationData":[OSD([sQuery(id+"F7.wireOp",EDGE,"E67")])]})]});
            fillet(context, id + "F14", {"entities" : qUnion([Q0, Q1, Q2, Q3, Q4, Q5]), "radius" : 3 * mm, "tangentPropagation" : true, "allowEdgeOverflow" : false});
        }
        {
            var Q0;
            Q0=makeQuery(id+"F1.opExtrude","CAP_EDGE",EDGE,{"disambiguationData":[OSD([sQuery(id+"F0.wireOp",EDGE,"E1.bottom")])],"isStart":false});
            fillet(context, id + "F15", {"entities" : qUnion([Q0]), "radius" : 2 * mm, "tangentPropagation" : true, "allowEdgeOverflow" : false});
        }
        {
            var Q0;
            {var subQ0=sQuery(id+"F0.wireOp",EDGE,"E22.filletArc");var subQ1=sQuery(id+"F0.wireOp",EDGE,"E7");var subQ2=sQuery(id+"F0.wireOp",EDGE,"E6");var subQ3=sQuery(id+"F0.wireOp",EDGE,"E5");var subQ4=sQuery(id+"F0.wireOp",EDGE,"E4");var subQ5=sQuery(id+"F0.wireOp",EDGE,"E1.bottom");var subQ6=sQuery(id+"F0.wireOp",EDGE,"E21.filletArc");var subQ7=sQuery(id+"F0.wireOp",EDGE,"E1.top");var subQ8=sQuery(id+"F0.wireOp",EDGE,"E1.left");var subQ9=sQuery(id+"F0.wireOp",EDGE,"E1.right");var subQ10=sQuery(id+"F0.wireOp",EDGE,"E23.filletArc");var subQ11=sQuery(id+"F0.wireOp",EDGE,"E24.filletArc");Q0=makeQuery(id+"F2.boolean.opBoolean","SPLIT",FACE,{"disambiguationData":[TD([makeQuery(id+"F1.opExtrude","SWEPT_FACE",FACE,{"disambiguationData":[OSD([subQ5])]})])],"derivedFrom":makeQuery(id+"F1.opExtrude","CAP_FACE",FACE,{"disambiguationData":[OSD([subQ5,subQ7,subQ8,subQ9,subQ4,subQ3,subQ2,subQ1,subQ6,subQ0,subQ10,subQ11])],"isStart":true})});}
            var sketch = newSketch(context, id + "F16", { "sketchPlane" : qUnion([Q0])});
            skSolve(sketch);
        }
        {
            var Q0;
            Q0=makeQuery(id+"F16.imprint","IMPRINT",FACE,{"disambiguationData":[TD([[makeQuery(id+"F16.imprint","IMPRINT",EDGE,{"derivedFrom":makeQuery(id+"F1.opExtrude","CAP_EDGE",EDGE,{"disambiguationData":[OSD([sQuery(id+"F0.wireOp",EDGE,"E1.bottom")])],"isStart":true})}),1.0]])]});
            var sketch = newSketch(context, id + "F17", { "sketchPlane" : qUnion([Q0])});
            skLineSegment(sketch, "E79", {"start": v(0, 74.25) * mm, "end": v(0, 104.25) * mm, "construction": true});
            skCircle(sketch, "E80", {"center": v(0, 104.25) * mm, "radius": 6 * mm});
            skLineSegment(sketch, "E81", {"start": v(-33, 74.25) * mm, "end": v(-15, 92.25) * mm});
            skLineSegment(sketch, "E82", {"start": v(33, 74.25) * mm, "end": v(15, 92.25) * mm});
            skLineSegment(sketch, "E83", {"start": v(15, 92.25) * mm, "end": v(15, 104.25) * mm});
            skLineSegment(sketch, "E84", {"start": v(-15, 92.25) * mm, "end": v(-15, 104.25) * mm});
            skArc(sketch, "E85", {"start": v(15, 104.25) * mm, "mid": v(0, 119.25) * mm, "end": v(-15, 104.25) * mm});
            skLineSegment(sketch, "E86", {"start": v(-74.24, 0) * mm, "end": v(73.89, 0) * mm, "construction": true});
            skLineSegment(sketch, "E87.MirrorCS", {"start": v(33, -74.25) * mm, "end": v(15, -92.25) * mm});
            skLineSegment(sketch, "E88.MirrorCS", {"start": v(15, -92.25) * mm, "end": v(15, -104.25) * mm});
            skLineSegment(sketch, "E89.MirrorCS", {"start": v(0, -74.25) * mm, "end": v(0, -104.25) * mm, "construction": true});
            skLineSegment(sketch, "E90.MirrorCS", {"start": v(-33, -74.25) * mm, "end": v(-15, -92.25) * mm});
            skArc(sketch, "E91.MirrorCS", {"start": v(15, -104.25) * mm, "mid": v(0, -119.25) * mm, "end": v(-15, -104.25) * mm});
            skLineSegment(sketch, "E92.MirrorCS", {"start": v(-15, -92.25) * mm, "end": v(-15, -104.25) * mm});
            skCircle(sketch, "E93.MirrorC", {"center": v(0, -104.25) * mm, "radius": 6 * mm});
            skSolve(sketch);
        }
        {
            var Q0;
            Q0=makeQuery(id+"F17.imprint","IMPRINT",FACE,{"disambiguationData":[TD([[makeQuery(id+"F17.imprint","IMPRINT",EDGE,{"derivedFrom":sQuery(id+"F17.wireOp",EDGE,"E80")}),-1.0]])]});
            var Q1;
            {var subQ1=sQuery(id+"F17.wireOp",EDGE,"E87.MirrorCS");Q1=makeQuery(id+"F17.imprint","IMPRINT",FACE,{"disambiguationData":[TD([[makeQuery(id+"F17.imprint","IMPRINT",EDGE,{"derivedFrom":subQ1}),-1.0]])]});}
            var Q2;
            Q2=makeQuery(id+"F16.imprint","IMPRINT",FACE,{"disambiguationData":[TD([[makeQuery(id+"F16.imprint","IMPRINT",EDGE,{"derivedFrom":makeQuery(id+"F1.opExtrude","CAP_EDGE",EDGE,{"disambiguationData":[OSD([sQuery(id+"F0.wireOp",EDGE,"E1.bottom")])],"isStart":true})}),1.0]])]});
            var Q3;
            Q3=makeQuery(id+"F2.opExtrude","CAP_FACE",FACE,{"disambiguationData":[OSD([sQuery(id+"F0.wireOp",EDGE,"E12"),sQuery(id+"F0.wireOp",EDGE,"E13"),sQuery(id+"F0.wireOp",EDGE,"E14"),sQuery(id+"F0.wireOp",EDGE,"E15"),sQuery(id+"F0.wireOp",EDGE,"E17.filletArc"),sQuery(id+"F0.wireOp",EDGE,"E18.filletArc"),sQuery(id+"F0.wireOp",EDGE,"E19.filletArc"),sQuery(id+"F0.wireOp",EDGE,"E20.filletArc"),sQuery(id+"F0.wireOp",EDGE,"E25.0"),sQuery(id+"F0.wireOp",EDGE,"E25.1"),sQuery(id+"F0.wireOp",EDGE,"E25.2"),sQuery(id+"F0.wireOp",EDGE,"E25.3"),sQuery(id+"F0.wireOp",EDGE,"E25.4"),sQuery(id+"F0.wireOp",EDGE,"E25.5"),sQuery(id+"F0.wireOp",EDGE,"E25.6"),sQuery(id+"F0.wireOp",EDGE,"E25.7")])],"isStart":false});
            extrude(context, id + "F18", {"entities" : qUnion([Q0, Q1, Q2]), "operationType" : NewBodyOperationType.ADD, "endBound" : BoundingType.UP_TO_SURFACE, "endBoundEntityFace" : qUnion([Q3]), "depth" : 25 * mm});
        }
    });
